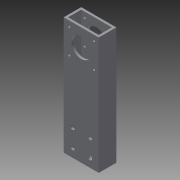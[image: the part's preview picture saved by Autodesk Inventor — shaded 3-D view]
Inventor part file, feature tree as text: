
AUTODESK INVENTOR PART (.ipt)
format: ipt  version: 2013 (Build 170138000, 138)  size: 135,168 bytes
history: native  units: in
note: dims shown in document units (in); Inventor stores cm internally (conversion verified against a paired STEP export)
features: extrude x3, sketch x3
ambient origin geometry x8: Origin, YZ Plane, XZ Plane, XY Plane, X Axis, Y Axis, Z Axis, Center Point
bodies: Solid1 (feature_tree)
feature tree (6):
  extrude  "Extrusion1"  Depth=6.688in
  extrude  "Extrusion2"  TaperAngle=90.0deg  [1 undecoded]
  extrude  "Extrusion3"  Depth=1.0in
  sketch  "Sketch1"  dims[d0=2.0in d1=6.688in]
  sketch  "Sketch2"  dims[d2=1.0in d3=90.0deg]
  sketch  "Sketch3"  dims[d4=1.125in d5=1.0in d6=45.0deg d7=2.0in d9=0.16in d10=0.16in d11=0.16in d12=0.16in d13=2.0in d14=1.5in d15=0.5in d16=180.0deg d17=1.0in d18=0.0in d19=0.25in d20=0.25in d21=1.0in d22=0.0in d23=0.125in d24=0.125in d25=1.75in d26=0.75in d27=10.0in d28=0.0in d29=1.0in d30=1.0in d31=0.25in d32=0.25in d33=1.0in d34=0.0in]
note: 1 required parameter value undecoded (feature->parameter linkage not recoverable at this tier; creation-order binding heuristic only, values carry confidence <= 0.55)
